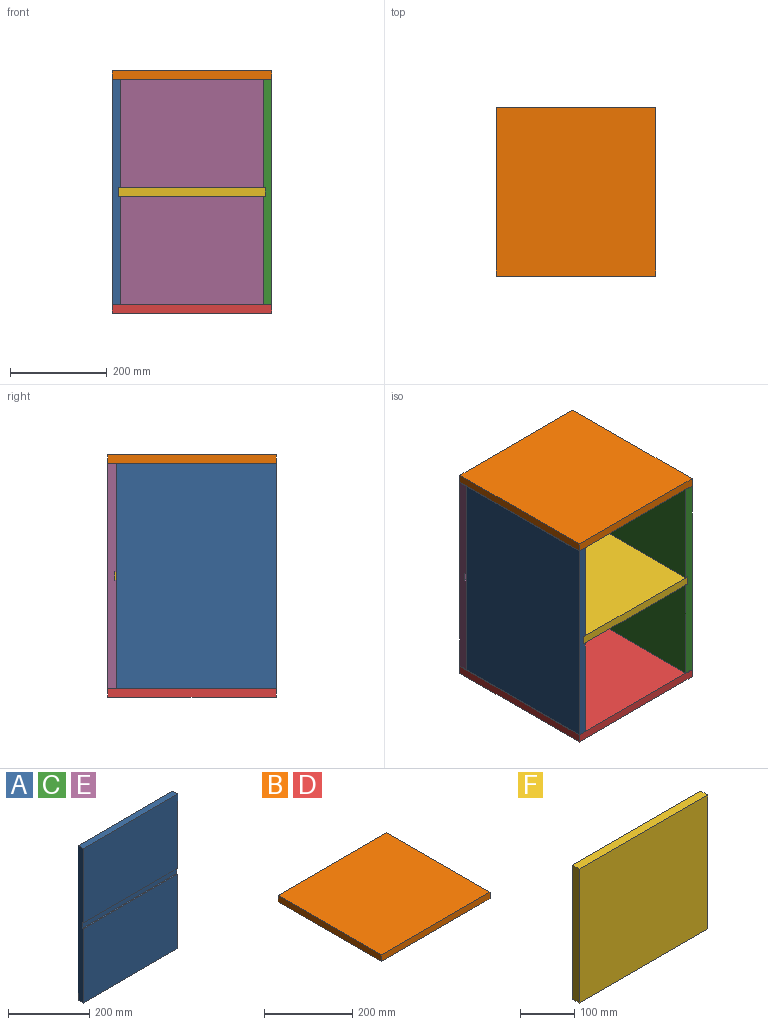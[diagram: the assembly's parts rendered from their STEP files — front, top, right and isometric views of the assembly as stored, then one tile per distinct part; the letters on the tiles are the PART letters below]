
ASSEMBLY  parts=6 mates=5
PART A: 10 faces, bbox 330x18x465 mm
  f0: plane 330x223.5mm, normal (0,-1,0), area 73755mm2, adj f1,f3,f4,f7
  f1: plane 465x18mm, normal (-1,0,0), area 8298mm2, adj f0,f2,f4,f5,f6,f7,f8,f9
  f2: plane 330x18mm, normal (0,0,-1), area 5940mm2, adj f1,f3,f5,f6
  f3: plane 465x18mm, normal (1,0,0), area 8298mm2, adj f0,f2,f4,f5,f6,f7,f8,f9
  f4: plane 330x18mm, normal (0,0,1), area 5940mm2, adj f0,f1,f3,f6
  f5: plane 330x223.5mm, normal (0,-1,0), area 73755mm2, adj f1,f2,f3,f8
  f6: plane 465x330mm, normal (0,1,0), area 153450mm2, adj f1,f2,f3,f4
  f7: plane 330x4mm, normal (0,0,-1), area 1320mm2, adj f0,f1,f3,f9
  f8: plane 330x4mm, normal (0,0,1), area 1320mm2, adj f1,f3,f5,f9
  f9: plane 330x18mm, normal (0,-1,0), area 5940mm2, adj f1,f3,f7,f8
PART B: 6 faces, bbox 348x330x18 mm
  f0: plane 330x18mm, normal (-1,0,0), area 5940mm2, adj f1,f3,f4,f5
  f1: plane 348x18mm, normal (0,-1,0), area 6264mm2, adj f0,f2,f4,f5
  f2: plane 330x18mm, normal (1,0,0), area 5940mm2, adj f1,f3,f4,f5
  f3: plane 348x18mm, normal (0,1,0), area 6264mm2, adj f0,f2,f4,f5
  f4: plane 348x330mm, normal (0,0,1), area 114840mm2, adj f0,f1,f2,f3
  f5: plane 348x330mm, normal (0,0,-1), area 114840mm2, adj f0,f1,f2,f3
PART C: same geometry as A
PART D: same geometry as B
PART E: same geometry as A
PART F: 6 faces, bbox 334x18x302 mm
  f0: plane 302x18mm, normal (-1,0,0), area 5436mm2, adj f1,f3,f4,f5
  f1: plane 334x18mm, normal (0,0,-1), area 6012mm2, adj f0,f2,f4,f5
  f2: plane 302x18mm, normal (1,0,0), area 5436mm2, adj f1,f3,f4,f5
  f3: plane 334x18mm, normal (0,0,1), area 6012mm2, adj f0,f2,f4,f5
  f4: plane 334x302mm, normal (0,-1,0), area 100868mm2, adj f0,f1,f2,f3
  f5: plane 334x302mm, normal (0,1,0), area 100868mm2, adj f0,f1,f2,f3
PLACE A rot(axis=(0,0,1),90deg) t=(0,-348,0)mm
PLACE B rot(axis=(0.71,0.71,0),180deg) t=(0,-348,483)mm
PLACE C rot(axis=(0,0,-1),90deg) t=(330,-18,0)mm
PLACE D rot(axis=(0.71,-0.71,0),180deg) t=(330,0,0)mm
PLACE E at identity fixed
PLACE F rot(axis=(-0.58,-0.58,0.58),120deg) t=(316,-348,223.5)mm
MATE fastened A.f3 <-> E.f0  axis (0,1,0) through (0,-18,465)mm
MATE fastened D.f5 <-> E.f2  axis (0,0,1) through (330,0,0)mm
MATE fastened B.f4 <-> E.f4  axis (0,0,-1) through (330,0,465)mm
MATE fastened E.f0 <-> C.f1  axis (0,-1,0) through (330,-18,465)mm
MATE fastened F.f2 <-> E.f9  axis (0,1,0) through (316,-14,241.5)mm
